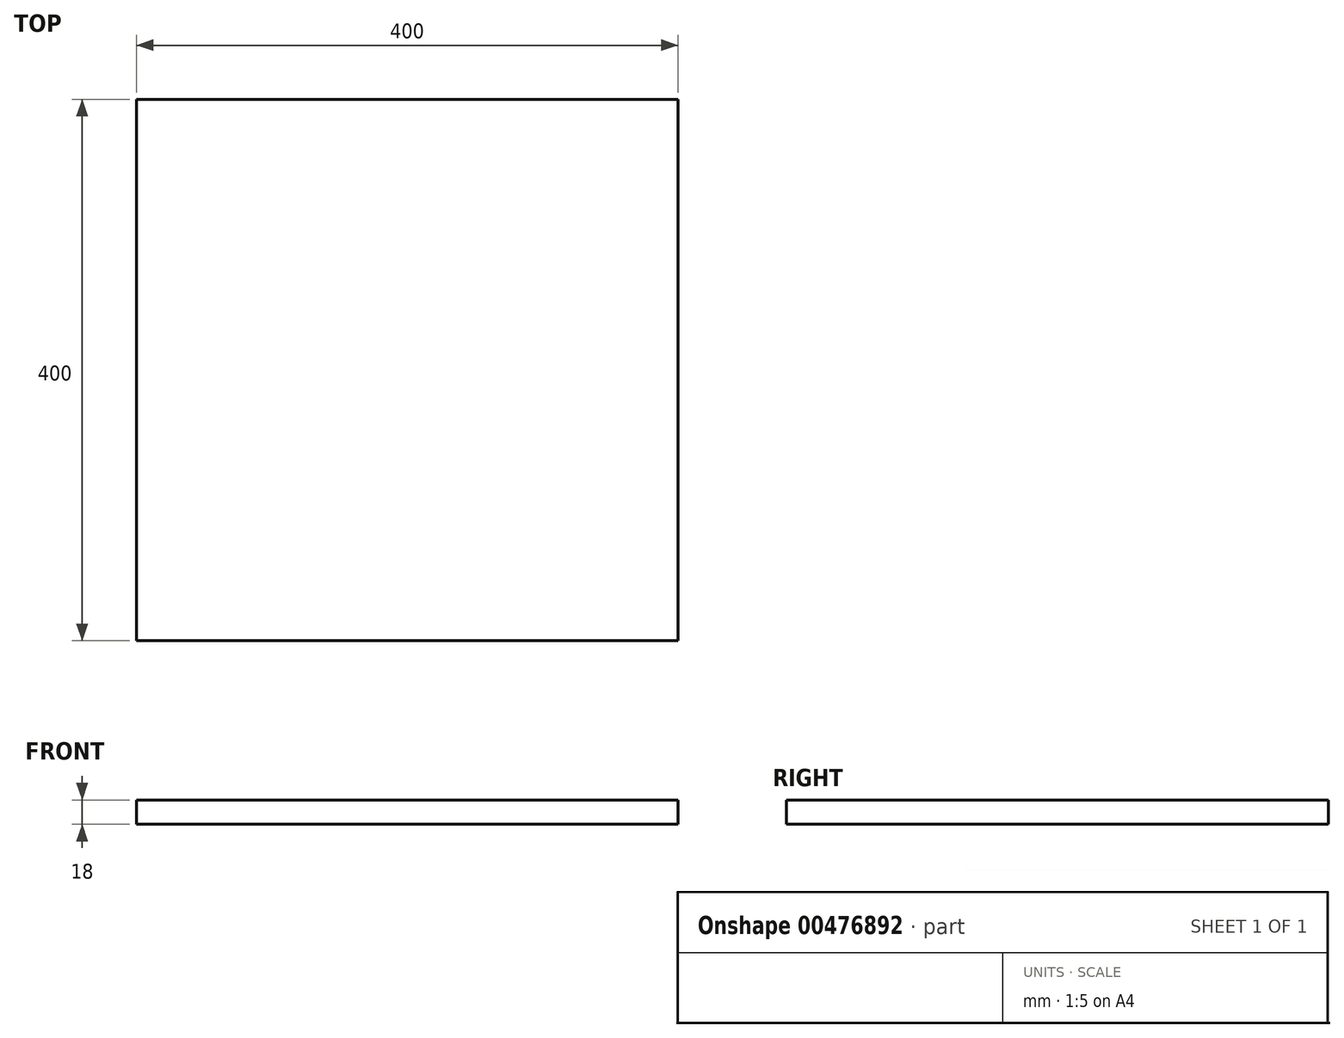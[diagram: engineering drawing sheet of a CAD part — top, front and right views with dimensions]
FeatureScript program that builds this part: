
annotation { "Feature Type Name" : "Feature", "Feature Type Description" : "" }
export const myFeature = defineFeature(function(context is Context, id is Id, definition is map)
    precondition{}
    {
        {
            var Q0;
            Q0=qCreatedBy(makeId("Top.planeOp"),FACE);
            var sketch = newSketch(context, id + "F0", { "sketchPlane" : qUnion([Q0])});
            skLineSegment(sketch, "E0.bottom", {"start": v(-134.19, 303.97) * mm, "end": v(265.81, 303.97) * mm});
            skLineSegment(sketch, "E0.top", {"start": v(-134.19, -96.03) * mm, "end": v(265.81, -96.03) * mm});
            skLineSegment(sketch, "E0.left", {"start": v(-134.19, 303.97) * mm, "end": v(-134.19, -96.03) * mm});
            skLineSegment(sketch, "E0.right", {"start": v(265.81, 303.97) * mm, "end": v(265.81, -96.03) * mm});
            skSolve(sketch);
        }
        {
            var Q0;
            Q0=qSketchRegion(id+"F0",true);
            extrude(context, id + "F1", {"entities" : qUnion([Q0]), "depth" : 18 * mm});
        }
    });
